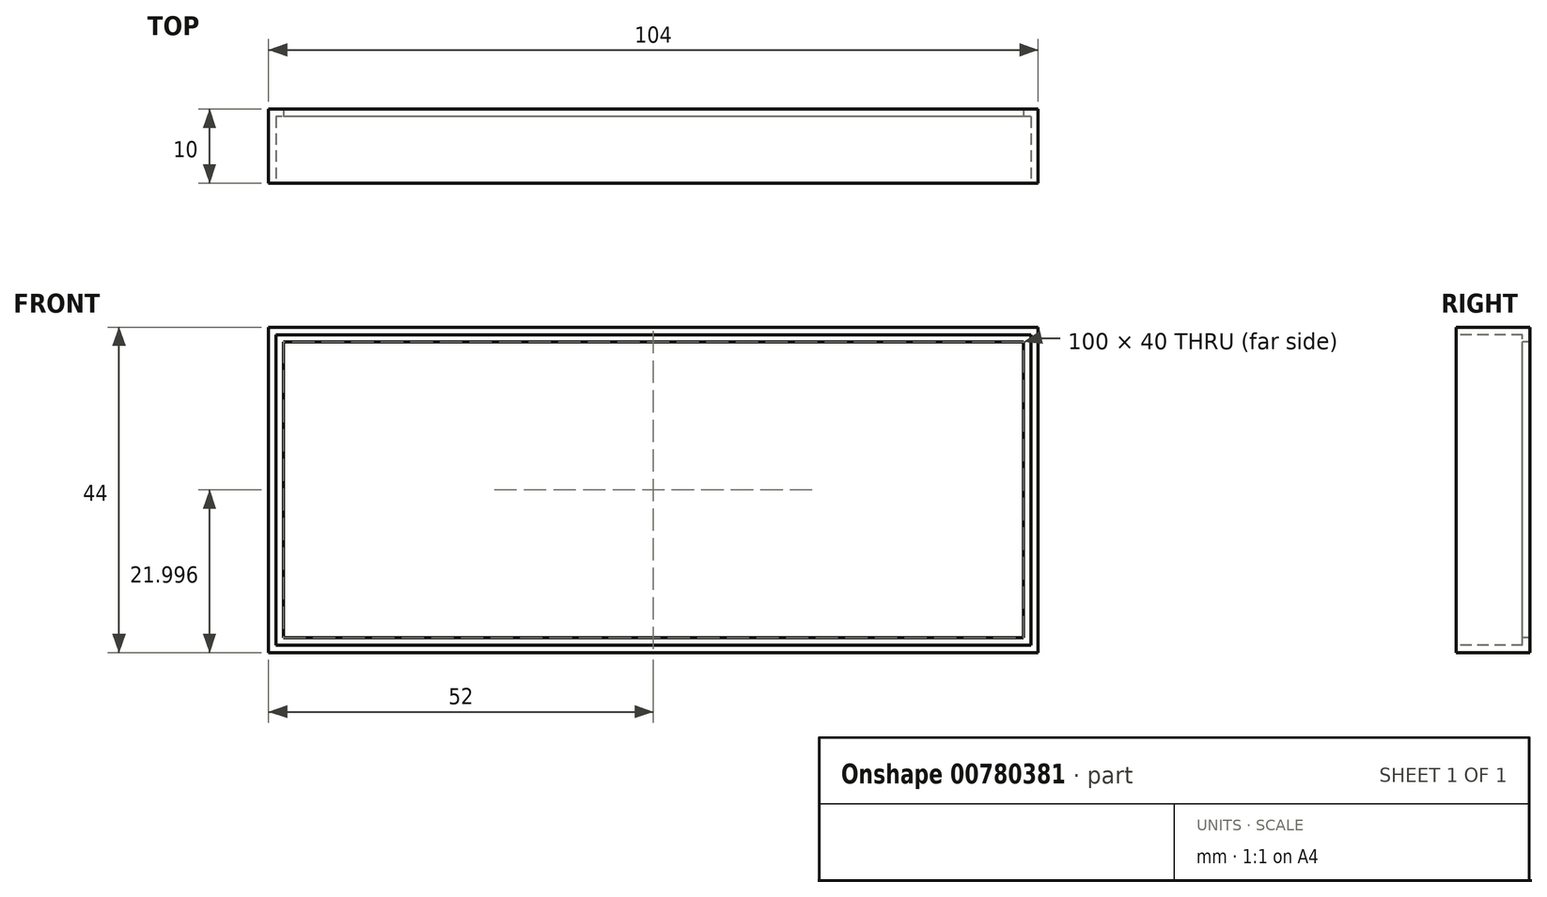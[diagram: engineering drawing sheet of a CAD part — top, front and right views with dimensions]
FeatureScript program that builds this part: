
annotation { "Feature Type Name" : "Feature", "Feature Type Description" : "" }
export const myFeature = defineFeature(function(context is Context, id is Id, definition is map)
    precondition{}
    {
        {
            var Q0;
            Q0=qCreatedBy(makeId("Front.planeOp"),FACE);
            var sketch = newSketch(context, id + "F0", { "sketchPlane" : qUnion([Q0])});
            skLineSegment(sketch, "E0.bottom", {"start": v(-49.89, 9.19) * mm, "end": v(-153.89, 9.19) * mm});
            skLineSegment(sketch, "E0.top", {"start": v(-49.89, 53.19) * mm, "end": v(-153.89, 53.19) * mm});
            skLineSegment(sketch, "E0.left", {"start": v(-49.89, 9.19) * mm, "end": v(-49.89, 53.19) * mm});
            skLineSegment(sketch, "E0.right", {"start": v(-153.89, 9.19) * mm, "end": v(-153.89, 53.19) * mm});
            skLineSegment(sketch, "E1.bottom", {"start": v(-51.89, 11.19) * mm, "end": v(-151.89, 11.19) * mm});
            skLineSegment(sketch, "E1.top", {"start": v(-51.89, 51.19) * mm, "end": v(-151.89, 51.19) * mm});
            skLineSegment(sketch, "E1.left", {"start": v(-51.89, 11.19) * mm, "end": v(-51.89, 51.19) * mm});
            skLineSegment(sketch, "E1.right", {"start": v(-151.89, 11.19) * mm, "end": v(-151.89, 51.19) * mm});
            skSolve(sketch);
        }
        {
            var Q0;
            Q0=makeQuery(id+"F0.imprint","IMPRINT",FACE,{"disambiguationData":[TD([[makeQuery(id+"F0.imprint","IMPRINT",EDGE,{"derivedFrom":sQuery(id+"F0.wireOp",EDGE,"E0.bottom")}),-1.0]])]});
            var Q1;
            Q1=makeQuery(id+"F0.imprint","IMPRINT",FACE,{"disambiguationData":[TD([[makeQuery(id+"F0.imprint","IMPRINT",EDGE,{"derivedFrom":sQuery(id+"F0.wireOp",EDGE,"E1.bottom")}),-1.0]])]});
            extrude(context, id + "F1", {"entities" : qUnion([Q0, Q1]), "oppositeDirection" : true, "depth" : 10 * mm, "offsetDistance" : 25 * mm});
        }
        {
            var Q0;
            Q0=makeQuery(id+"F1.opExtrude","CAP_FACE",FACE,{"disambiguationData":[OSD([sQuery(id+"F0.wireOp",EDGE,"E0.bottom"),sQuery(id+"F0.wireOp",EDGE,"E0.top"),sQuery(id+"F0.wireOp",EDGE,"E0.left"),sQuery(id+"F0.wireOp",EDGE,"E0.right")])],"isStart":true});
            shell(context, id + "F2", {"entities" : qUnion([Q0]), "thickness" : 1 * mm});
        }
        {
            var Q0;
            Q0=makeQuery(id+"F0.imprint","IMPRINT",FACE,{"disambiguationData":[TD([[makeQuery(id+"F0.imprint","IMPRINT",EDGE,{"derivedFrom":sQuery(id+"F0.wireOp",EDGE,"E1.bottom")}),-1.0]])]});
            extrude(context, id + "F3", {"entities" : qUnion([Q0]), "operationType" : NewBodyOperationType.REMOVE, "oppositeDirection" : true, "depth" : 25 * mm, "offsetDistance" : 25 * mm});
        }
    });
